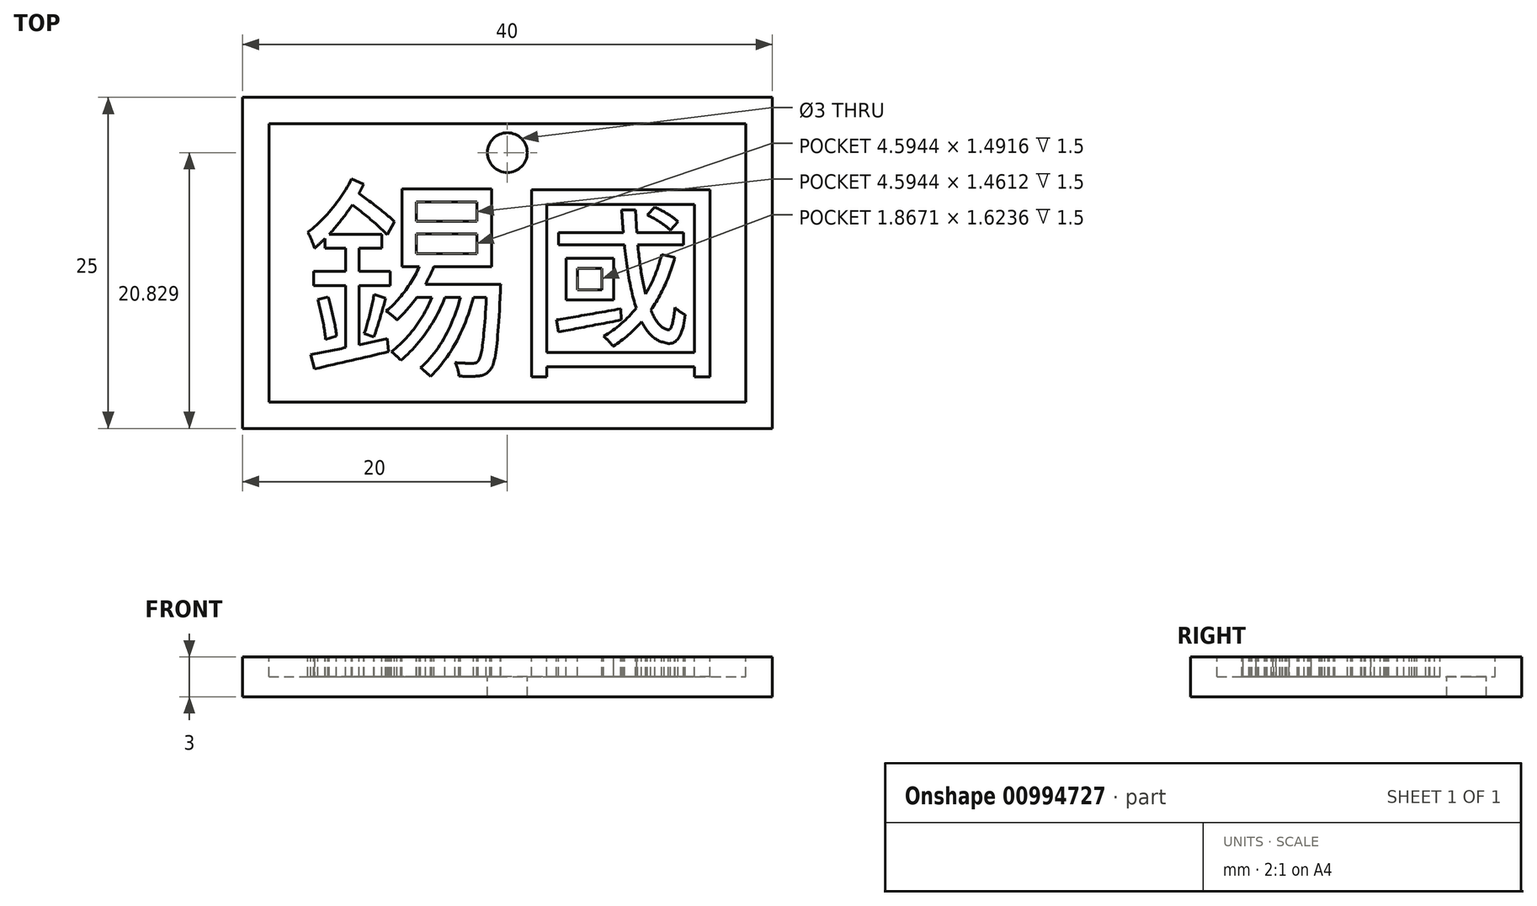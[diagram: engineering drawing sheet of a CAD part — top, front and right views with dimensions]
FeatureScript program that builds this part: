
annotation { "Feature Type Name" : "Feature", "Feature Type Description" : "" }
export const myFeature = defineFeature(function(context is Context, id is Id, definition is map)
    precondition{}
    {
        {
            var Q0;
            Q0=qCreatedBy(makeId("Top.planeOp"),FACE);
            var sketch = newSketch(context, id + "F0", { "sketchPlane" : qUnion([Q0])});
            skLineSegment(sketch, "E0.bottom", {"start": v(20, -12.5) * mm, "end": v(-20, -12.5) * mm});
            skLineSegment(sketch, "E0.top", {"start": v(20, 12.5) * mm, "end": v(-20, 12.5) * mm});
            skLineSegment(sketch, "E0.left", {"start": v(20, -12.5) * mm, "end": v(20, 12.5) * mm});
            skLineSegment(sketch, "E0.right", {"start": v(-20, -12.5) * mm, "end": v(-20, 12.5) * mm});
            skPoint(sketch, "E0.middle", {"position": v(0, 0) * mm});
            skSolve(sketch);
        }
        {
            var Q0;
            Q0 = qSketchRegion(id + "F0", true);
            extrude(context, id + "F1", {"entities" : qUnion([Q0]), "oppositeDirection" : true, "depth" : 3 * mm, "offsetDistance" : 25 * mm});
        }
        {
            var Q0;
            Q0=makeQuery(id+"F1.opExtrude","CAP_FACE",FACE,{"disambiguationData":[OSD([sQuery(id+"F0.wireOp",EDGE,"E0.bottom"),sQuery(id+"F0.wireOp",EDGE,"E0.top"),sQuery(id+"F0.wireOp",EDGE,"E0.left"),sQuery(id+"F0.wireOp",EDGE,"E0.right")])],"isStart":true});
            var sketch = newSketch(context, id + "F2", { "sketchPlane" : qUnion([Q0])});
            skLineSegment(sketch, "E1.0", {"start": v(18, -10.5) * mm, "end": v(18, 10.5) * mm});
            skLineSegment(sketch, "E1.1", {"start": v(-18, -10.5) * mm, "end": v(18, -10.5) * mm});
            skLineSegment(sketch, "E1.2", {"start": v(-18, 10.5) * mm, "end": v(-18, -10.5) * mm});
            skLineSegment(sketch, "E1.3", {"start": v(18, 10.5) * mm, "end": v(-18, 10.5) * mm});
            skSolve(sketch);
        }
        {
            var Q0;
            Q0 = qSketchRegion(id + "F2", true);
            extrude(context, id + "F3", {"entities" : qUnion([Q0]), "operationType" : NewBodyOperationType.REMOVE, "oppositeDirection" : true, "depth" : 1.5 * mm, "offsetDistance" : 25 * mm});
        }
        {
            var Q0;
            Q0=makeQuery(id+"F3.boolean.opBoolean","COPY",FACE,{"derivedFrom":makeQuery(id+"F3.opExtrude","CAP_FACE",FACE,{"disambiguationData":[OSD([sQuery(id+"F2.wireOp",EDGE,"E1.0"),sQuery(id+"F2.wireOp",EDGE,"E1.1"),sQuery(id+"F2.wireOp",EDGE,"E1.2"),sQuery(id+"F2.wireOp",EDGE,"E1.3")])],"isStart":false})});
            var sketch = newSketch(context, id + "F4", { "sketchPlane" : qUnion([Q0])});
            skCircle(sketch, "E2", {"center": v(0, 8.33) * mm, "radius": 1.5 * mm});
            skSolve(sketch);
        }
        {
            var Q0;
            Q0=makeQuery(id+"F4.imprint","IMPRINT",FACE,{"disambiguationData":[TD([[makeQuery(id+"F4.imprint","IMPRINT",EDGE,{"derivedFrom":sQuery(id+"F4.wireOp",EDGE,"E2")}),-1.0]])]});
            var sketch = newSketch(context, id + "F5", { "sketchPlane" : qUnion([Q0])});
            skSolve(sketch);
        }
        {
            var Q0;
            Q0 = qSketchRegion(id + "F5", true);
            var Q1;
            Q1=makeQuery(id+"F4.imprint","IMPRINT",FACE,{"disambiguationData":[TD([[makeQuery(id+"F4.imprint","IMPRINT",EDGE,{"derivedFrom":sQuery(id+"F4.wireOp",EDGE,"E2")}),1.0]])]});
            extrude(context, id + "F6", {"entities" : qUnion([Q0, Q1]), "operationType" : NewBodyOperationType.REMOVE, "endBound" : BoundingType.THROUGH_ALL, "oppositeDirection" : true, "depth" : 25 * mm, "offsetDistance" : 25 * mm});
        }
        {
            var Q0;
            Q0=qCreatedBy(makeId("Top.planeOp"),FACE);
            var sketch = newSketch(context, id + "F7", { "sketchPlane" : qUnion([Q0])});
            skText(sketch, "E3", { "text": "錫國", "fontName": "NotoSansCJKtc-Regular.otf"});
            const initialGuessF7  = {"E3": [-0.0158, -0.00732, 1, 0, 0.01169]};
            skSetInitialGuess(sketch, initialGuessF7);
            skSolve(sketch);
        }
        {
            var Q0;
            Q0 = qSketchRegion(id + "F7", true);
            var Q1;
            Q1=makeQuery(id+"F7.imprint","IMPRINT",FACE,{"disambiguationData":[TD([[makeQuery(id+"F7.imprint","IMPRINT",EDGE,{"derivedFrom":sQuery(id+"F7.wireOp",EDGE,"E3.sketch_text.stroke-88")}),1.0]])]});
            var Q2;
            Q2=makeQuery(id+"F7.imprint","IMPRINT",FACE,{"disambiguationData":[TD([[makeQuery(id+"F7.imprint","IMPRINT",EDGE,{"derivedFrom":sQuery(id+"F7.wireOp",EDGE,"E3.sketch_text.stroke-72")}),1.0]])]});
            var Q3;
            Q3=makeQuery(id+"F7.imprint","IMPRINT",FACE,{"disambiguationData":[TD([[makeQuery(id+"F7.imprint","IMPRINT",EDGE,{"derivedFrom":sQuery(id+"F7.wireOp",EDGE,"E3.sketch_text.stroke-80")}),1.0]])]});
            var Q4;
            Q4=makeQuery(id+"F7.imprint","IMPRINT",FACE,{"disambiguationData":[TD([[makeQuery(id+"F7.imprint","IMPRINT",EDGE,{"derivedFrom":sQuery(id+"F7.wireOp",EDGE,"E3.sketch_text.stroke-76")}),1.0]])]});
            extrude(context, id + "F8", {"entities" : qUnion([Q0, Q1, Q2, Q3, Q4]), "operationType" : NewBodyOperationType.ADD, "oppositeDirection" : true, "depth" : 1.5 * mm, "offsetDistance" : 25 * mm});
        }
    });
